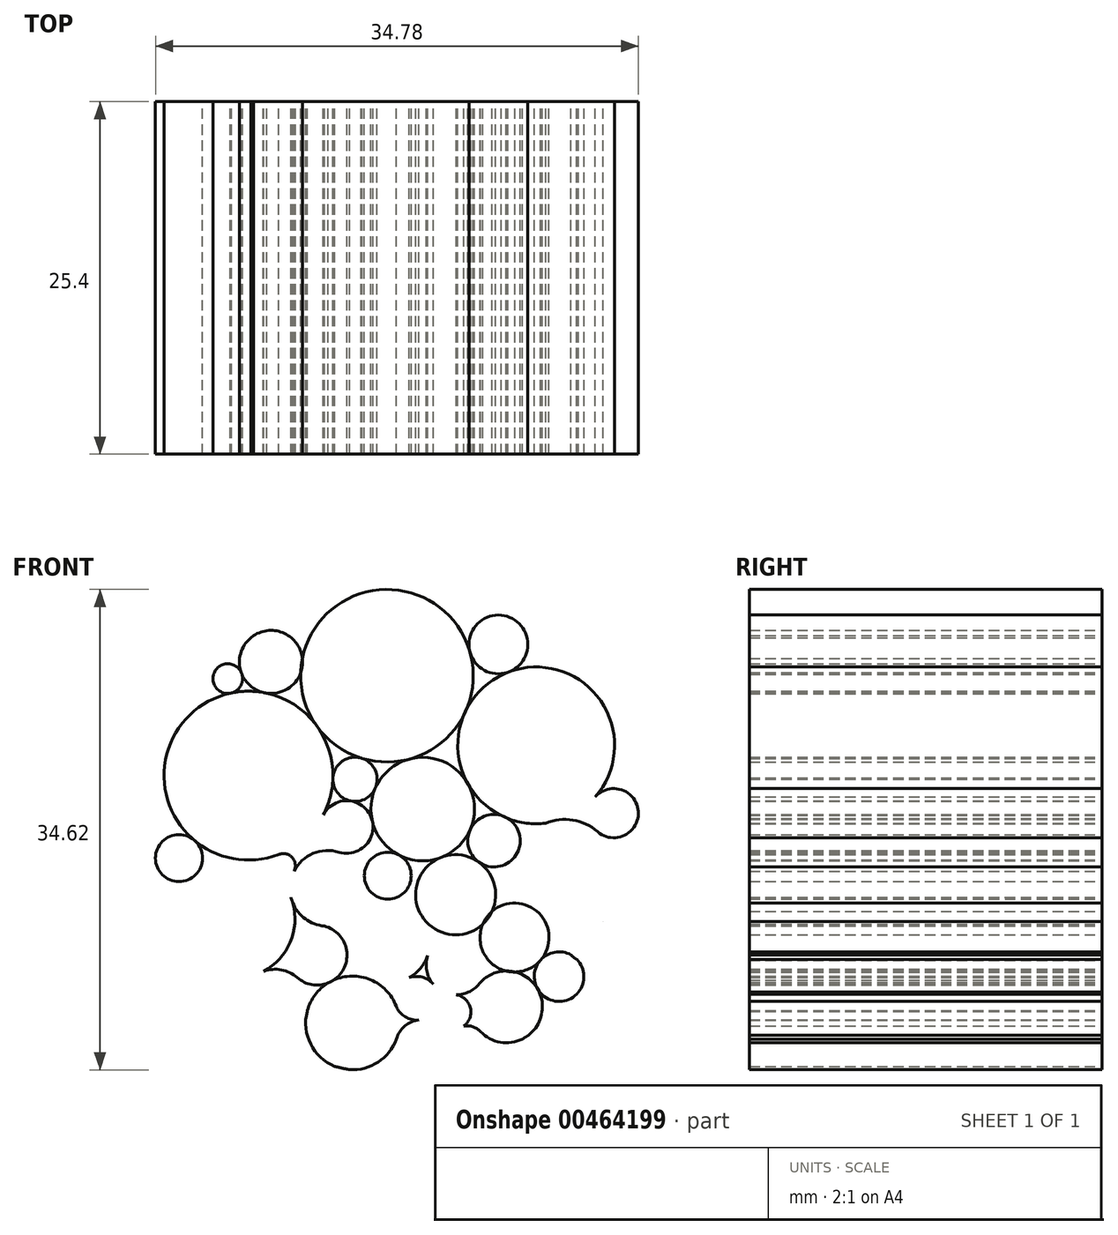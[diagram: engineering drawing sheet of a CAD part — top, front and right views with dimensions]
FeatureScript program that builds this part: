
annotation { "Feature Type Name" : "Feature", "Feature Type Description" : "" }
export const myFeature = defineFeature(function(context is Context, id is Id, definition is map)
    precondition{}
    {
        {
            var Q0;
            Q0=qCreatedBy(makeId("Front.planeOp"),FACE);
            var sketch = newSketch(context, id + "F0", { "sketchPlane" : qUnion([Q0])});
            skCircle(sketch, "E0", {"center": v(0, 0) * mm, "radius": 17.48 * mm});
            skCircle(sketch, "E1", {"center": v(-0.69, 11.24) * mm, "radius": 6.22 * mm});
            skPoint(sketch, "E1.first.point", {"position": v(-1.07, 17.45) * mm});
            skPoint(sketch, "E1.second.point", {"position": v(-1.07, 17.45) * mm});
            skPoint(sketch, "E1.third.point", {"position": v(-4.77, 6.55) * mm});
            skCircle(sketch, "E2", {"center": v(10.06, 6.22) * mm, "radius": 5.65 * mm});
            skPoint(sketch, "E2.first.point", {"position": v(4.95, 8.61) * mm});
            skPoint(sketch, "E2.second.point", {"position": v(14.87, 9.2) * mm});
            skPoint(sketch, "E2.third.point", {"position": v(14.57, 2.83) * mm});
            skCircle(sketch, "E3", {"center": v(-10.66, 4.04) * mm, "radius": 6.08 * mm});
            skPoint(sketch, "E3.first.point", {"position": v(-5.73, 7.6) * mm});
            skPoint(sketch, "E3.second.point", {"position": v(-16.34, 6.2) * mm});
            skPoint(sketch, "E3.third.point", {"position": v(-12.26, -1.83) * mm});
            skCircle(sketch, "E4", {"center": v(7.34, 13.5) * mm, "radius": 2.12 * mm});
            skPoint(sketch, "E4.first.point", {"position": v(5.3, 12.92) * mm});
            skPoint(sketch, "E4.second.point", {"position": v(8.35, 15.36) * mm});
            skPoint(sketch, "E4.third.point", {"position": v(8.08, 11.51) * mm});
            skPoint(sketch, "E5.first.point", {"position": v(-5.7, 7.56) * mm});
            skPoint(sketch, "E5.second.point", {"position": v(-5.76, 7.65) * mm});
            skPoint(sketch, "E5.third.point", {"position": v(1.19, 18) * mm});
            skPoint(sketch, "E6.first.point", {"position": v(6.16, 10.3) * mm});
            skPoint(sketch, "E6.second.point", {"position": v(6.27, 10.59) * mm});
            skPoint(sketch, "E6.third.point", {"position": v(5.93, 10.25) * mm});
            skCircle(sketch, "E7", {"center": v(-9.04, 12.23) * mm, "radius": 2.27 * mm});
            skPoint(sketch, "E7.first.point", {"position": v(-10.5, 13.98) * mm});
            skPoint(sketch, "E7.second.point", {"position": v(-6.78, 12.49) * mm});
            skPoint(sketch, "E7.third.point", {"position": v(-9.61, 10.03) * mm});
            skPoint(sketch, "E8.first.point", {"position": v(-15.2, 0) * mm});
            skPoint(sketch, "E8.second.point", {"position": v(-15.37, -8.33) * mm});
            skPoint(sketch, "E8.third.point", {"position": v(-10.1, -2.02) * mm});
            skCircle(sketch, "E9", {"center": v(-11.6, -6.28) * mm, "radius": 4.29 * mm});
            skPoint(sketch, "E9.first.point", {"position": v(-11.21, -2.02) * mm});
            skCircle(sketch, "E10", {"center": v(-15.67, -1.9) * mm, "radius": 1.7 * mm});
            skPoint(sketch, "E10.first.point", {"position": v(-17.35, -2.1) * mm});
            skPoint(sketch, "E10.second.point", {"position": v(-14.58, -0.6) * mm});
            skPoint(sketch, "E10.third.point", {"position": v(-14.52, -3.14) * mm});
            skPoint(sketch, "E11.first.point", {"position": v(-6.03, 0.1) * mm});
            skPoint(sketch, "E11.second.point", {"position": v(0, 5.06) * mm});
            skPoint(sketch, "E11.third.point", {"position": v(5, 3.73) * mm});
            skPoint(sketch, "E12.first.point", {"position": v(-5.12, 6.55) * mm});
            skPoint(sketch, "E12.second.point", {"position": v(-0.4, 5.03) * mm});
            skPoint(sketch, "E12.third.point", {"position": v(-0.3, 2.46) * mm});
            skPoint(sketch, "E13.second.point", {"position": v(5.22, 13.18) * mm});
            skPoint(sketch, "E13.third.point", {"position": v(3.75, 6.88) * mm});
            skPoint(sketch, "E14.first.point", {"position": v(4.66, 8.06) * mm});
            skPoint(sketch, "E14.second.point", {"position": v(-6.9, 11.24) * mm});
            skPoint(sketch, "E14.third.point", {"position": v(4.29, -4.32) * mm});
            skPoint(sketch, "E15.second.point", {"position": v(-0.6, 17.46) * mm});
            skPoint(sketch, "E15.third.point", {"position": v(4.2, 7.4) * mm});
            skPoint(sketch, "E16.first.point", {"position": v(-2.87, 5.42) * mm});
            skPoint(sketch, "E16.second.point", {"position": v(-0.68, -2.43) * mm});
            skPoint(sketch, "E16.third.point", {"position": v(1.85, 0.39) * mm});
            skCircle(sketch, "E17", {"center": v(-8.74, -12.3) * mm, "radius": 2.4 * mm});
            skPoint(sketch, "E17.first.point", {"position": v(-9.95, -10.24) * mm});
            skPoint(sketch, "E17.second.point", {"position": v(-10.12, -14.25) * mm});
            skPoint(sketch, "E17.third.point", {"position": v(-6.4, -11.81) * mm});
            skCircle(sketch, "E18", {"center": v(-5.72, -8.9) * mm, "radius": 2.16 * mm});
            skPoint(sketch, "E18.first.point", {"position": v(-7.77, -8.2) * mm});
            skPoint(sketch, "E18.second.point", {"position": v(-7.15, -10.51) * mm});
            skPoint(sketch, "E18.third.point", {"position": v(-3.73, -9.72) * mm});
            skCircle(sketch, "E19", {"center": v(-4.95, -4.08) * mm, "radius": 2.73 * mm});
            skPoint(sketch, "E19.first.point", {"position": v(-7.6, -4.74) * mm});
            skPoint(sketch, "E19.second.point", {"position": v(-5.2, -6.8) * mm});
            skPoint(sketch, "E19.third.point", {"position": v(-2.32, -4.81) * mm});
            skCircle(sketch, "E20", {"center": v(-8.16, -2.45) * mm, "radius": 0.87 * mm});
            skPoint(sketch, "E20.first.point", {"position": v(-8.44, -1.62) * mm});
            skPoint(sketch, "E20.second.point", {"position": v(-8.74, -3.1) * mm});
            skPoint(sketch, "E20.third.point", {"position": v(-7.38, -2.84) * mm});
            skCircle(sketch, "E21", {"center": v(-3.6, 0.34) * mm, "radius": 1.9 * mm});
            skPoint(sketch, "E21.first.point", {"position": v(-5.27, 1.22) * mm});
            skPoint(sketch, "E21.second.point", {"position": v(-4.15, -1.47) * mm});
            skPoint(sketch, "E21.third.point", {"position": v(-2.28, 1.7) * mm});
            skPoint(sketch, "E22.first.point", {"position": v(-3.48, 5.68) * mm});
            skPoint(sketch, "E22.second.point", {"position": v(-4.58, 3.87) * mm});
            skPoint(sketch, "E22.third.point", {"position": v(-3.26, 2.2) * mm});
            skCircle(sketch, "E23", {"center": v(-2.99, 3.78) * mm, "radius": 1.6 * mm});
            skPoint(sketch, "E23.first.point", {"position": v(-2.55, 5.31) * mm});
            skPoint(sketch, "E24.second.point", {"position": v(-7.6, -4.76) * mm});
            skPoint(sketch, "E24.third.point", {"position": v(-3.07, -6.06) * mm});
            skPoint(sketch, "E25.first.point", {"position": v(-1.57, 17.4) * mm});
            skPoint(sketch, "E25.third.point", {"position": v(3.15, 6.35) * mm});
            skCircle(sketch, "E26", {"center": v(1.89, 1.63) * mm, "radius": 3.73 * mm});
            skPoint(sketch, "E26.first.point", {"position": v(-1.53, 3.13) * mm});
            skPoint(sketch, "E26.second.point", {"position": v(0.92, 5.24) * mm});
            skPoint(sketch, "E26.third.point", {"position": v(5.24, 0) * mm});
            skCircle(sketch, "E27", {"center": v(-0.63, -3.17) * mm, "radius": 1.69 * mm});
            skPoint(sketch, "E27.first.point", {"position": v(-2.28, -3.52) * mm});
            skPoint(sketch, "E27.second.point", {"position": v(0.16, -1.67) * mm});
            skPoint(sketch, "E27.third.point", {"position": v(0.77, -4.12) * mm});
            skCircle(sketch, "E28", {"center": v(7.02, -0.65) * mm, "radius": 1.89 * mm});
            skPoint(sketch, "E28.first.point", {"position": v(5.3, 0.12) * mm});
            skPoint(sketch, "E28.second.point", {"position": v(8.02, 0.96) * mm});
            skPoint(sketch, "E28.third.point", {"position": v(8.4, -1.94) * mm});
            skCircle(sketch, "E29", {"center": v(12.11, -2.72) * mm, "radius": 3.6 * mm});
            skPoint(sketch, "E29.first.point", {"position": v(11.9, 0.88) * mm});
            skPoint(sketch, "E29.second.point", {"position": v(8.77, -1.36) * mm});
            skPoint(sketch, "E29.third.point", {"position": v(14.8, -5.13) * mm});
            skCircle(sketch, "E30", {"center": v(15.65, 1.34) * mm, "radius": 1.77 * mm});
            skPoint(sketch, "E30.first.point", {"position": v(14.31, 2.5) * mm});
            skPoint(sketch, "E30.second.point", {"position": v(14.48, 0) * mm});
            skPoint(sketch, "E30.third.point", {"position": v(17.42, 1.49) * mm});
            skCircle(sketch, "E31", {"center": v(-12.15, 11.03) * mm, "radius": 1.07 * mm});
            skPoint(sketch, "E31.first.point", {"position": v(-12.94, 11.75) * mm});
            skPoint(sketch, "E31.second.point", {"position": v(-11.19, 11.48) * mm});
            skPoint(sketch, "E31.third.point", {"position": v(-11.99, 9.97) * mm});
            skCircle(sketch, "E32", {"center": v(13.79, -7.73) * mm, "radius": 1.67 * mm});
            skPoint(sketch, "E32.first.point", {"position": v(13.26, -6.14) * mm});
            skPoint(sketch, "E32.second.point", {"position": v(15.25, -8.55) * mm});
            skPoint(sketch, "E32.third.point", {"position": v(13.3, -9.33) * mm});
            skCircle(sketch, "E33", {"center": v(15.5, -5.76) * mm, "radius": 0.94 * mm});
            skPoint(sketch, "E33.second.point", {"position": v(16.39, -6.09) * mm});
            skPoint(sketch, "E33.third.point", {"position": v(14.9, -6.48) * mm});
            skCircle(sketch, "E34", {"center": v(4.26, -4.54) * mm, "radius": 2.89 * mm});
            skPoint(sketch, "E34.first.point", {"position": v(3.23, -1.85) * mm});
            skPoint(sketch, "E34.second.point", {"position": v(4.98, -1.75) * mm});
            skPoint(sketch, "E34.third.point", {"position": v(1.9, -6.19) * mm});
            skCircle(sketch, "E35", {"center": v(-0.62, -7.9) * mm, "radius": 3.04 * mm});
            skPoint(sketch, "E35.first.point", {"position": v(-0.63, -4.86) * mm});
            skPoint(sketch, "E35.second.point", {"position": v(-2.9, -5.89) * mm});
            skCircle(sketch, "E36", {"center": v(-3.17, -13.78) * mm, "radius": 3.37 * mm});
            skPoint(sketch, "E36.first.point", {"position": v(-4.92, -10.9) * mm});
            skPoint(sketch, "E36.second.point", {"position": v(-6.44, -12.95) * mm});
            skPoint(sketch, "E36.third.point", {"position": v(-1.83, -10.69) * mm});
            skPoint(sketch, "E37.first.point", {"position": v(1.37, -10.2) * mm});
            skPoint(sketch, "E37.second.point", {"position": v(0, -12.63) * mm});
            skPoint(sketch, "E37.third.point", {"position": v(7.04, -16) * mm});
            skPoint(sketch, "E38.first.point", {"position": v(8.76, -4.04) * mm});
            skPoint(sketch, "E38.second.point", {"position": v(6.89, -5.75) * mm});
            skPoint(sketch, "E38.third.point", {"position": v(10.43, -10.8) * mm});
            skCircle(sketch, "E39", {"center": v(4.3, -9.59) * mm, "radius": 2.16 * mm});
            skPoint(sketch, "E39.first.point", {"position": v(4.29, -7.43) * mm});
            skPoint(sketch, "E39.second.point", {"position": v(2.26, -8.85) * mm});
            skPoint(sketch, "E39.third.point", {"position": v(5.4, -11.45) * mm});
            skCircle(sketch, "E40", {"center": v(1.45, -12) * mm, "radius": 1.57 * mm});
            skPoint(sketch, "E40.first.point", {"position": v(0.56, -10.7) * mm});
            skPoint(sketch, "E40.second.point", {"position": v(-0.02, -12.57) * mm});
            skPoint(sketch, "E40.third.point", {"position": v(2.65, -10.98) * mm});
            skCircle(sketch, "E41", {"center": v(8.5, -7.63) * mm, "radius": 2.48 * mm});
            skPoint(sketch, "E41.second.point", {"position": v(9.98, -5.63) * mm});
            skPoint(sketch, "E41.third.point", {"position": v(9.36, -9.96) * mm});
            skCircle(sketch, "E42", {"center": v(1.84, -15.46) * mm, "radius": 1.9 * mm});
            skPoint(sketch, "E42.first.point", {"position": v(1.62, -13.56) * mm});
            skPoint(sketch, "E42.second.point", {"position": v(0, -14.94) * mm});
            skPoint(sketch, "E42.third.point", {"position": v(2.06, -17.36) * mm});
            skCircle(sketch, "E43", {"center": v(11.71, -10.44) * mm, "radius": 1.79 * mm});
            skPoint(sketch, "E43.first.point", {"position": v(10.37, -9.27) * mm});
            skPoint(sketch, "E43.second.point", {"position": v(12.57, -8.87) * mm});
            skPoint(sketch, "E43.third.point", {"position": v(12.98, -11.7) * mm});
            skCircle(sketch, "E44", {"center": v(7.93, -12.62) * mm, "radius": 2.58 * mm});
            skPoint(sketch, "E44.first.point", {"position": v(5.84, -11.1) * mm});
            skPoint(sketch, "E44.second.point", {"position": v(8.53, -10.11) * mm});
            skPoint(sketch, "E44.third.point", {"position": v(9.08, -14.94) * mm});
            skCircle(sketch, "E45", {"center": v(4.1, -13) * mm, "radius": 1.26 * mm});
            skPoint(sketch, "E45.first.point", {"position": v(4.3, -11.75) * mm});
            skPoint(sketch, "E45.second.point", {"position": v(2.94, -12.49) * mm});
            skPoint(sketch, "E45.third.point", {"position": v(4.3, -14.24) * mm});
            skPoint(sketch, "E46.second.point", {"position": v(5.5, -16.6) * mm});
            skPoint(sketch, "E46.third.point", {"position": v(5.32, -16.65) * mm});
            skCircle(sketch, "E47", {"center": v(5.08, -15.32) * mm, "radius": 1.34 * mm});
            skPoint(sketch, "E47.second.point", {"position": v(6.05, -14.4) * mm});
            skSolve(sketch);
        }
        {
            var Q0;
            {var subQ0=sQuery(id+"F0.wireOp",EDGE,"E1");var subQ3=sQuery(id+"F0.wireOp",EDGE,"E7");var subQ4=makeQuery(id+"F0.imprint","INTERSECT",VERTEX,{"disambiguationData":[OD(0.0)],"derivedFrom":[subQ3,subQ0]});Q0=makeQuery(id+"F0.imprint","IMPRINT",FACE,{"disambiguationData":[TD([[makeQuery(id+"F0.imprint","IMPRINT",EDGE,{"disambiguationData":[TD([[subQ4,1.0]])],"derivedFrom":subQ3}),-1.0]])]});}
            var Q1;
            {var subQ0=sQuery(id+"F0.wireOp",EDGE,"E7");var subQ1=sQuery(id+"F0.wireOp",EDGE,"E0");var subQ5=makeQuery(id+"F0.imprint","INTERSECT",VERTEX,{"disambiguationData":[OD(0.0)],"derivedFrom":[subQ1,subQ0]});Q1=makeQuery(id+"F0.imprint","IMPRINT",FACE,{"disambiguationData":[TD([[makeQuery(id+"F0.imprint","IMPRINT",EDGE,{"disambiguationData":[TD([[subQ5,-1.0]])],"derivedFrom":subQ1}),1.0]])]});}
            var Q2;
            {var subQ0=sQuery(id+"F0.wireOp",EDGE,"E31");var subQ5=sQuery(id+"F0.wireOp",EDGE,"E3");var subQ7=makeQuery(id+"F0.imprint","INTERSECT",VERTEX,{"disambiguationData":[OD(0.0)],"derivedFrom":[subQ5,subQ0]});Q2=makeQuery(id+"F0.imprint","IMPRINT",FACE,{"disambiguationData":[TD([[makeQuery(id+"F0.imprint","IMPRINT",EDGE,{"disambiguationData":[TD([[subQ7,-1.0]])],"derivedFrom":subQ5}),-1.0]])]});}
            var Q3;
            {var subQ0=sQuery(id+"F0.wireOp",EDGE,"E3");var subQ4=sQuery(id+"F0.wireOp",EDGE,"E7");var subQ5=makeQuery(id+"F0.imprint","INTERSECT",VERTEX,{"disambiguationData":[OD(0.0)],"derivedFrom":[subQ0,subQ4]});Q3=makeQuery(id+"F0.imprint","IMPRINT",FACE,{"disambiguationData":[TD([[makeQuery(id+"F0.imprint","IMPRINT",EDGE,{"disambiguationData":[TD([[subQ5,1.0]])],"derivedFrom":subQ0}),1.0]])]});}
            var Q4;
            {var subQ0=sQuery(id+"F0.wireOp",EDGE,"E23");var subQ3=sQuery(id+"F0.wireOp",EDGE,"E3");var subQ7=makeQuery(id+"F0.imprint","INTERSECT",VERTEX,{"disambiguationData":[OD(0.0)],"derivedFrom":[subQ3,subQ0]});Q4=makeQuery(id+"F0.imprint","IMPRINT",FACE,{"disambiguationData":[TD([[makeQuery(id+"F0.imprint","IMPRINT",EDGE,{"disambiguationData":[TD([[subQ7,-1.0]])],"derivedFrom":subQ3}),-1.0]])]});}
            var Q5;
            {var subQ0=sQuery(id+"F0.wireOp",EDGE,"E21");var subQ1=makeQuery(id+"F0.imprint","INTERSECT",VERTEX,{"derivedFrom":[subQ0,sQuery(id+"F0.wireOp",EDGE,"E23")]});Q5=makeQuery(id+"F0.imprint","IMPRINT",FACE,{"disambiguationData":[TD([[makeQuery(id+"F0.imprint","IMPRINT",EDGE,{"disambiguationData":[TD([[subQ1,1.0]])],"derivedFrom":subQ0}),1.0]])]});}
            var Q6;
            {var subQ0=sQuery(id+"F0.wireOp",EDGE,"E20");var subQ1=sQuery(id+"F0.wireOp",EDGE,"E3");var subQ2=makeQuery(id+"F0.imprint","INTERSECT",VERTEX,{"disambiguationData":[OD(0.0)],"derivedFrom":[subQ1,subQ0]});Q6=makeQuery(id+"F0.imprint","IMPRINT",FACE,{"disambiguationData":[TD([[makeQuery(id+"F0.imprint","IMPRINT",EDGE,{"disambiguationData":[TD([[subQ2,-1.0]])],"derivedFrom":subQ1}),-1.0]])]});}
            var Q7;
            {var subQ0=sQuery(id+"F0.wireOp",EDGE,"E9");var subQ8=sQuery(id+"F0.wireOp",EDGE,"E19");var subQ9=makeQuery(id+"F0.imprint","INTERSECT",VERTEX,{"disambiguationData":[OD(0.0)],"derivedFrom":[subQ0,subQ8]});Q7=makeQuery(id+"F0.imprint","IMPRINT",FACE,{"disambiguationData":[TD([[makeQuery(id+"F0.imprint","IMPRINT",EDGE,{"disambiguationData":[TD([[subQ9,-1.0]])],"derivedFrom":subQ0}),1.0]])]});}
            var Q8;
            {var subQ0=sQuery(id+"F0.wireOp",EDGE,"E10");var subQ1=makeQuery(id+"F0.imprint","INTERSECT",VERTEX,{"derivedFrom":[sQuery(id+"F0.wireOp",EDGE,"E0"),subQ0]});Q8=makeQuery(id+"F0.imprint","IMPRINT",FACE,{"disambiguationData":[TD([[makeQuery(id+"F0.imprint","IMPRINT",EDGE,{"disambiguationData":[TD([[subQ1,1.0]])],"derivedFrom":subQ0}),1.0]])]});}
            var Q9;
            {var subQ0=sQuery(id+"F0.wireOp",EDGE,"E19");var subQ7=sQuery(id+"F0.wireOp",EDGE,"E9");var subQ8=makeQuery(id+"F0.imprint","INTERSECT",VERTEX,{"disambiguationData":[OD(0.0)],"derivedFrom":[subQ7,subQ0]});Q9=makeQuery(id+"F0.imprint","IMPRINT",FACE,{"disambiguationData":[TD([[makeQuery(id+"F0.imprint","IMPRINT",EDGE,{"disambiguationData":[TD([[subQ8,1.0]])],"derivedFrom":subQ7}),-1.0]])]});}
            var Q10;
            {var subQ0=sQuery(id+"F0.wireOp",EDGE,"E27");var subQ1=makeQuery(id+"F0.imprint","INTERSECT",VERTEX,{"derivedFrom":[sQuery(id+"F0.wireOp",EDGE,"E19"),subQ0]});Q10=makeQuery(id+"F0.imprint","IMPRINT",FACE,{"disambiguationData":[TD([[makeQuery(id+"F0.imprint","IMPRINT",EDGE,{"disambiguationData":[TD([[subQ1,1.0]])],"derivedFrom":subQ0}),1.0]])]});}
            var Q11;
            {var subQ0=sQuery(id+"F0.wireOp",EDGE,"E26");var subQ5=makeQuery(id+"F0.imprint","INTERSECT",VERTEX,{"derivedFrom":[sQuery(id+"F0.wireOp",EDGE,"E2"),subQ0]});Q11=makeQuery(id+"F0.imprint","IMPRINT",FACE,{"disambiguationData":[TD([[makeQuery(id+"F0.imprint","IMPRINT",EDGE,{"disambiguationData":[TD([[subQ5,-1.0]])],"derivedFrom":subQ0}),1.0]])]});}
            var Q12;
            {var subQ0=sQuery(id+"F0.wireOp",EDGE,"E2");var subQ7=makeQuery(id+"F0.imprint","INTERSECT",VERTEX,{"derivedFrom":[sQuery(id+"F0.wireOp",EDGE,"E0"),subQ0]});Q12=makeQuery(id+"F0.imprint","IMPRINT",FACE,{"disambiguationData":[TD([[makeQuery(id+"F0.imprint","IMPRINT",EDGE,{"disambiguationData":[TD([[subQ7,-1.0]])],"derivedFrom":subQ0}),1.0]])]});}
            var Q13;
            {var subQ0=sQuery(id+"F0.wireOp",EDGE,"E29");var subQ3=sQuery(id+"F0.wireOp",EDGE,"E2");var subQ4=makeQuery(id+"F0.imprint","INTERSECT",VERTEX,{"disambiguationData":[OD(0.0)],"derivedFrom":[subQ3,subQ0]});Q13=makeQuery(id+"F0.imprint","IMPRINT",FACE,{"disambiguationData":[TD([[makeQuery(id+"F0.imprint","IMPRINT",EDGE,{"disambiguationData":[TD([[subQ4,-1.0]])],"derivedFrom":subQ3}),-1.0]])]});}
            var Q14;
            {var subQ0=sQuery(id+"F0.wireOp",EDGE,"E28");var subQ3=sQuery(id+"F0.wireOp",EDGE,"E2");var subQ4=makeQuery(id+"F0.imprint","INTERSECT",VERTEX,{"disambiguationData":[OD(0.0)],"derivedFrom":[subQ3,subQ0]});Q14=makeQuery(id+"F0.imprint","IMPRINT",FACE,{"disambiguationData":[TD([[makeQuery(id+"F0.imprint","IMPRINT",EDGE,{"disambiguationData":[TD([[subQ4,-1.0]])],"derivedFrom":subQ3}),-1.0]])]});}
            var Q15;
            {var subQ1=sQuery(id+"F0.wireOp",EDGE,"E34");var subQ9=makeQuery(id+"F0.imprint","INTERSECT",VERTEX,{"derivedFrom":[sQuery(id+"F0.wireOp",EDGE,"E26"),subQ1]});Q15=makeQuery(id+"F0.imprint","IMPRINT",FACE,{"disambiguationData":[TD([[makeQuery(id+"F0.imprint","IMPRINT",EDGE,{"disambiguationData":[TD([[subQ9,1.0]])],"derivedFrom":subQ1}),1.0]])]});}
            var Q16;
            {var subQ0=sQuery(id+"F0.wireOp",EDGE,"E35");var subQ4=sQuery(id+"F0.wireOp",EDGE,"E34");var subQ5=makeQuery(id+"F0.imprint","INTERSECT",VERTEX,{"disambiguationData":[OD(0.0)],"derivedFrom":[subQ4,subQ0]});Q16=makeQuery(id+"F0.imprint","IMPRINT",FACE,{"disambiguationData":[TD([[makeQuery(id+"F0.imprint","IMPRINT",EDGE,{"disambiguationData":[TD([[subQ5,1.0]])],"derivedFrom":subQ0}),1.0]])]});}
            var Q17;
            {var subQ0=sQuery(id+"F0.wireOp",EDGE,"E18");var subQ1=sQuery(id+"F0.wireOp",EDGE,"E9");var subQ2=makeQuery(id+"F0.imprint","INTERSECT",VERTEX,{"disambiguationData":[OD(0.0)],"derivedFrom":[subQ1,subQ0]});Q17=makeQuery(id+"F0.imprint","IMPRINT",FACE,{"disambiguationData":[TD([[makeQuery(id+"F0.imprint","IMPRINT",EDGE,{"disambiguationData":[TD([[subQ2,-1.0]])],"derivedFrom":subQ1}),-1.0]])]});}
            var Q18;
            {var subQ0=sQuery(id+"F0.wireOp",EDGE,"E17");var subQ2=sQuery(id+"F0.wireOp",EDGE,"E9");var subQ3=makeQuery(id+"F0.imprint","INTERSECT",VERTEX,{"disambiguationData":[OD(0.0)],"derivedFrom":[subQ2,subQ0]});Q18=makeQuery(id+"F0.imprint","IMPRINT",FACE,{"disambiguationData":[TD([[makeQuery(id+"F0.imprint","IMPRINT",EDGE,{"disambiguationData":[TD([[subQ3,-1.0]])],"derivedFrom":subQ2}),-1.0]])]});}
            var Q19;
            {var subQ0=sQuery(id+"F0.wireOp",EDGE,"E36");var subQ6=sQuery(id+"F0.wireOp",EDGE,"E0");var subQ7=makeQuery(id+"F0.imprint","INTERSECT",VERTEX,{"disambiguationData":[OD(0.0)],"derivedFrom":[subQ6,subQ0]});Q19=makeQuery(id+"F0.imprint","IMPRINT",FACE,{"disambiguationData":[TD([[makeQuery(id+"F0.imprint","IMPRINT",EDGE,{"disambiguationData":[TD([[subQ7,-1.0]])],"derivedFrom":subQ6}),1.0]])]});}
            var Q20;
            {var subQ0=sQuery(id+"F0.wireOp",EDGE,"E40");var subQ3=sQuery(id+"F0.wireOp",EDGE,"E35");var subQ4=makeQuery(id+"F0.imprint","INTERSECT",VERTEX,{"disambiguationData":[OD(0.0)],"derivedFrom":[subQ3,subQ0]});Q20=makeQuery(id+"F0.imprint","IMPRINT",FACE,{"disambiguationData":[TD([[makeQuery(id+"F0.imprint","IMPRINT",EDGE,{"disambiguationData":[TD([[subQ4,-1.0]])],"derivedFrom":subQ3}),-1.0]])]});}
            var Q21;
            {var subQ0=sQuery(id+"F0.wireOp",EDGE,"E42");var subQ2=sQuery(id+"F0.wireOp",EDGE,"E36");var subQ3=makeQuery(id+"F0.imprint","INTERSECT",VERTEX,{"disambiguationData":[OD(0.0)],"derivedFrom":[subQ2,subQ0]});Q21=makeQuery(id+"F0.imprint","IMPRINT",FACE,{"disambiguationData":[TD([[makeQuery(id+"F0.imprint","IMPRINT",EDGE,{"disambiguationData":[TD([[subQ3,-1.0]])],"derivedFrom":subQ2}),-1.0]])]});}
            var Q22;
            {var subQ0=sQuery(id+"F0.wireOp",EDGE,"E47");var subQ2=sQuery(id+"F0.wireOp",EDGE,"E45");var subQ3=makeQuery(id+"F0.imprint","INTERSECT",VERTEX,{"disambiguationData":[OD(0.0)],"derivedFrom":[subQ2,subQ0]});Q22=makeQuery(id+"F0.imprint","IMPRINT",FACE,{"disambiguationData":[TD([[makeQuery(id+"F0.imprint","IMPRINT",EDGE,{"disambiguationData":[TD([[subQ3,-1.0]])],"derivedFrom":subQ2}),-1.0]])]});}
            var Q23;
            {var subQ0=sQuery(id+"F0.wireOp",EDGE,"E45");var subQ1=sQuery(id+"F0.wireOp",EDGE,"E39");var subQ2=makeQuery(id+"F0.imprint","INTERSECT",VERTEX,{"disambiguationData":[OD(0.0)],"derivedFrom":[subQ1,subQ0]});Q23=makeQuery(id+"F0.imprint","IMPRINT",FACE,{"disambiguationData":[TD([[makeQuery(id+"F0.imprint","IMPRINT",EDGE,{"disambiguationData":[TD([[subQ2,-1.0]])],"derivedFrom":subQ1}),-1.0]])]});}
            var Q24;
            {var subQ0=sQuery(id+"F0.wireOp",EDGE,"E44");var subQ10=sQuery(id+"F0.wireOp",EDGE,"E0");var subQ11=makeQuery(id+"F0.imprint","INTERSECT",VERTEX,{"disambiguationData":[OD(0.0)],"derivedFrom":[subQ10,subQ0]});Q24=makeQuery(id+"F0.imprint","IMPRINT",FACE,{"disambiguationData":[TD([[makeQuery(id+"F0.imprint","IMPRINT",EDGE,{"disambiguationData":[TD([[subQ11,-1.0]])],"derivedFrom":subQ10}),1.0]])]});}
            var Q25;
            {var subQ0=sQuery(id+"F0.wireOp",EDGE,"E33");var subQ1=sQuery(id+"F0.wireOp",EDGE,"E32");var subQ2=makeQuery(id+"F0.imprint","INTERSECT",VERTEX,{"disambiguationData":[OD(0.0)],"derivedFrom":[subQ1,subQ0]});Q25=makeQuery(id+"F0.imprint","IMPRINT",FACE,{"disambiguationData":[TD([[makeQuery(id+"F0.imprint","IMPRINT",EDGE,{"disambiguationData":[TD([[subQ2,1.0]])],"derivedFrom":subQ0}),1.0]])]});}
            var Q26;
            {var subQ0=sQuery(id+"F0.wireOp",EDGE,"E43");var subQ6=sQuery(id+"F0.wireOp",EDGE,"E0");var subQ7=makeQuery(id+"F0.imprint","INTERSECT",VERTEX,{"disambiguationData":[OD(0.0)],"derivedFrom":[subQ6,subQ0]});Q26=makeQuery(id+"F0.imprint","IMPRINT",FACE,{"disambiguationData":[TD([[makeQuery(id+"F0.imprint","IMPRINT",EDGE,{"disambiguationData":[TD([[subQ7,-1.0]])],"derivedFrom":subQ6}),1.0]])]});}
            var Q27;
            {var subQ0=sQuery(id+"F0.wireOp",EDGE,"E41");var subQ7=sQuery(id+"F0.wireOp",EDGE,"E34");var subQ8=makeQuery(id+"F0.imprint","INTERSECT",VERTEX,{"disambiguationData":[OD(0.0)],"derivedFrom":[subQ7,subQ0]});Q27=makeQuery(id+"F0.imprint","IMPRINT",FACE,{"disambiguationData":[TD([[makeQuery(id+"F0.imprint","IMPRINT",EDGE,{"disambiguationData":[TD([[subQ8,-1.0]])],"derivedFrom":subQ7}),-1.0]])]});}
            var Q28;
            {var subQ0=sQuery(id+"F0.wireOp",EDGE,"E32");var subQ2=sQuery(id+"F0.wireOp",EDGE,"E33");var subQ8=makeQuery(id+"F0.imprint","INTERSECT",VERTEX,{"disambiguationData":[OD(0.0)],"derivedFrom":[subQ0,subQ2]});Q28=makeQuery(id+"F0.imprint","IMPRINT",FACE,{"disambiguationData":[TD([[makeQuery(id+"F0.imprint","IMPRINT",EDGE,{"disambiguationData":[TD([[subQ8,-1.0]])],"derivedFrom":subQ0}),1.0]])]});}
            var Q29;
            {var subQ0=sQuery(id+"F0.wireOp",EDGE,"E30");var subQ1=makeQuery(id+"F0.imprint","INTERSECT",VERTEX,{"derivedFrom":[sQuery(id+"F0.wireOp",EDGE,"E0"),subQ0]});Q29=makeQuery(id+"F0.imprint","IMPRINT",FACE,{"disambiguationData":[TD([[makeQuery(id+"F0.imprint","IMPRINT",EDGE,{"disambiguationData":[TD([[subQ1,-1.0]])],"derivedFrom":subQ0}),1.0]])]});}
            var Q30;
            {var subQ0=sQuery(id+"F0.wireOp",EDGE,"E4");var subQ1=makeQuery(id+"F0.imprint","INTERSECT",VERTEX,{"derivedFrom":[sQuery(id+"F0.wireOp",EDGE,"E0"),subQ0]});Q30=makeQuery(id+"F0.imprint","IMPRINT",FACE,{"disambiguationData":[TD([[makeQuery(id+"F0.imprint","IMPRINT",EDGE,{"disambiguationData":[TD([[subQ1,-1.0]])],"derivedFrom":subQ0}),1.0]])]});}
            extrude(context, id + "F1", {"entities" : qUnion([Q0, Q1, Q2, Q3, Q4, Q5, Q6, Q7, Q8, Q9, Q10, Q11, Q12, Q13, Q14, Q15, Q16, Q17, Q18, Q19, Q20, Q21, Q22, Q23, Q24, Q25, Q26, Q27, Q28, Q29, Q30]), "depth" : 25.4 * mm});
        }
    });
